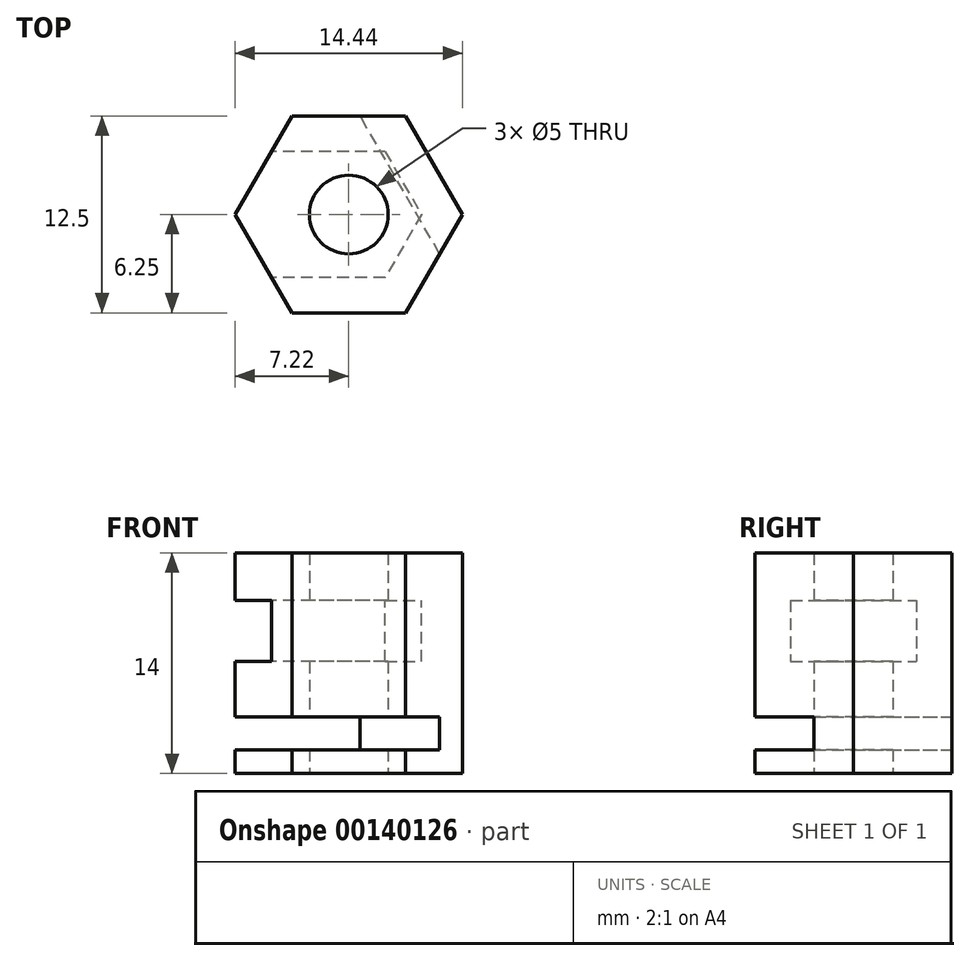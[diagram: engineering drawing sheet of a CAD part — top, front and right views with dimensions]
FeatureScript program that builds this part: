
annotation { "Feature Type Name" : "Feature", "Feature Type Description" : "" }
export const myFeature = defineFeature(function(context is Context, id is Id, definition is map)
    precondition{}
    {
        {
            var Q0;
            Q0=qCreatedBy(makeId("Top.planeOp"),FACE);
            var sketch = newSketch(context, id + "F0", { "sketchPlane" : qUnion([Q0])});
            skCircle(sketch, "E0.cCircle", {"center": v(0, 0) * mm, "radius": 6.25 * mm, "construction": true});
            skLineSegment(sketch, "E0.0", {"start": v(3.6, -6.25) * mm, "end": v(-3.6, -6.25) * mm});
            skLineSegment(sketch, "E0.1", {"start": v(-3.6, -6.25) * mm, "end": v(-7.22, 0) * mm});
            skLineSegment(sketch, "E0.2", {"start": v(-7.22, 0) * mm, "end": v(-3.6, 6.25) * mm});
            skLineSegment(sketch, "E0.3", {"start": v(-3.6, 6.25) * mm, "end": v(3.6, 6.25) * mm});
            skLineSegment(sketch, "E0.4", {"start": v(3.6, 6.25) * mm, "end": v(7.22, 0) * mm});
            skLineSegment(sketch, "E0.5", {"start": v(7.22, 0) * mm, "end": v(3.6, -6.25) * mm});
            skPoint(sketch, "E0.0.midPoint", {"position": v(0, -6.25) * mm});
            skCircle(sketch, "E1", {"center": v(0, 0) * mm, "radius": 2.5 * mm});
            skSolve(sketch);
        }
        {
            var Q0;
            Q0 = qSketchRegion(id + "F0", true);
            extrude(context, id + "F1", {"entities" : qUnion([Q0]), "depth" : 14 * mm});
        }
        {
            var Q0;
            Q0=makeQuery(id+"F1.opExtrude","SWEPT_FACE",FACE,{"disambiguationData":[OSD([sQuery(id+"F0.wireOp",EDGE,"E0.1")])]});
            var sketch = newSketch(context, id + "F2", { "sketchPlane" : qUnion([Q0])});
            skLineSegment(sketch, "E2.bottom", {"start": v(8.74, 1.5) * mm, "end": v(-8.74, 1.5) * mm});
            skLineSegment(sketch, "E2.top", {"start": v(8.74, 3.6) * mm, "end": v(-8.74, 3.6) * mm});
            skLineSegment(sketch, "E2.left", {"start": v(8.74, 1.5) * mm, "end": v(8.74, 3.6) * mm});
            skLineSegment(sketch, "E2.right", {"start": v(-8.74, 1.5) * mm, "end": v(-8.74, 3.6) * mm});
            skPoint(sketch, "E2.middle", {"position": v(0, 2.55) * mm});
            skSolve(sketch);
        }
        {
            var Q0;
            Q0 = qSketchRegion(id + "F2", true);
            extrude(context, id + "F3", {"entities" : qUnion([Q0]), "operationType" : NewBodyOperationType.REMOVE, "oppositeDirection" : true, "depth" : 10 * mm});
        }
        {
            var Q0;
            Q0=makeQuery(id+"F1.opExtrude","CAP_FACE",FACE,{"disambiguationData":[OSD([sQuery(id+"F0.wireOp",EDGE,"E0.0"),sQuery(id+"F0.wireOp",EDGE,"E0.1"),sQuery(id+"F0.wireOp",EDGE,"E0.2"),sQuery(id+"F0.wireOp",EDGE,"E0.3"),sQuery(id+"F0.wireOp",EDGE,"E0.4"),sQuery(id+"F0.wireOp",EDGE,"E0.5"),sQuery(id+"F0.wireOp",EDGE,"E1")])],"isStart":false});
            var sketch = newSketch(context, id + "F4", { "sketchPlane" : qUnion([Q0])});
            skCircle(sketch, "E3.cCircle", {"center": v(0, 0) * mm, "radius": 4 * mm, "construction": true});
            skLineSegment(sketch, "E3.2", {"start": v(-2.3, 4) * mm, "end": v(2.3, 4) * mm});
            skLineSegment(sketch, "E3.3", {"start": v(2.3, 4) * mm, "end": v(4.62, 0) * mm});
            skLineSegment(sketch, "E3.4", {"start": v(4.62, 0) * mm, "end": v(2.3, -4) * mm});
            skLineSegment(sketch, "E3.5", {"start": v(2.3, -4) * mm, "end": v(-2.3, -4) * mm});
            skPoint(sketch, "E3.0.midPoint", {"position": v(-3.46, -2) * mm});
            skLineSegment(sketch, "E4", {"start": v(-2.3, 4) * mm, "end": v(-10.69, 4) * mm});
            skLineSegment(sketch, "E5", {"start": v(-2.3, -4) * mm, "end": v(-10.33, -4) * mm});
            skLineSegment(sketch, "E6", {"start": v(-10.33, -4) * mm, "end": v(-10.69, 4) * mm});
            skPoint(sketch, "E7.orphan", {"position": v(-4.62, 0) * mm});
            skSolve(sketch);
        }
        {
            var Q0;
            Q0 = qSketchRegion(id + "F4", true);
            extrude(context, id + "F5", {"entities" : qUnion([Q0]), "operationType" : NewBodyOperationType.REMOVE, "oppositeDirection" : true, "depth" : 6.9 * mm, "hasSecondDirection" : true, "secondDirectionOppositeDirection" : true, "secondDirectionDepth" : 3 * mm});
        }
    });
